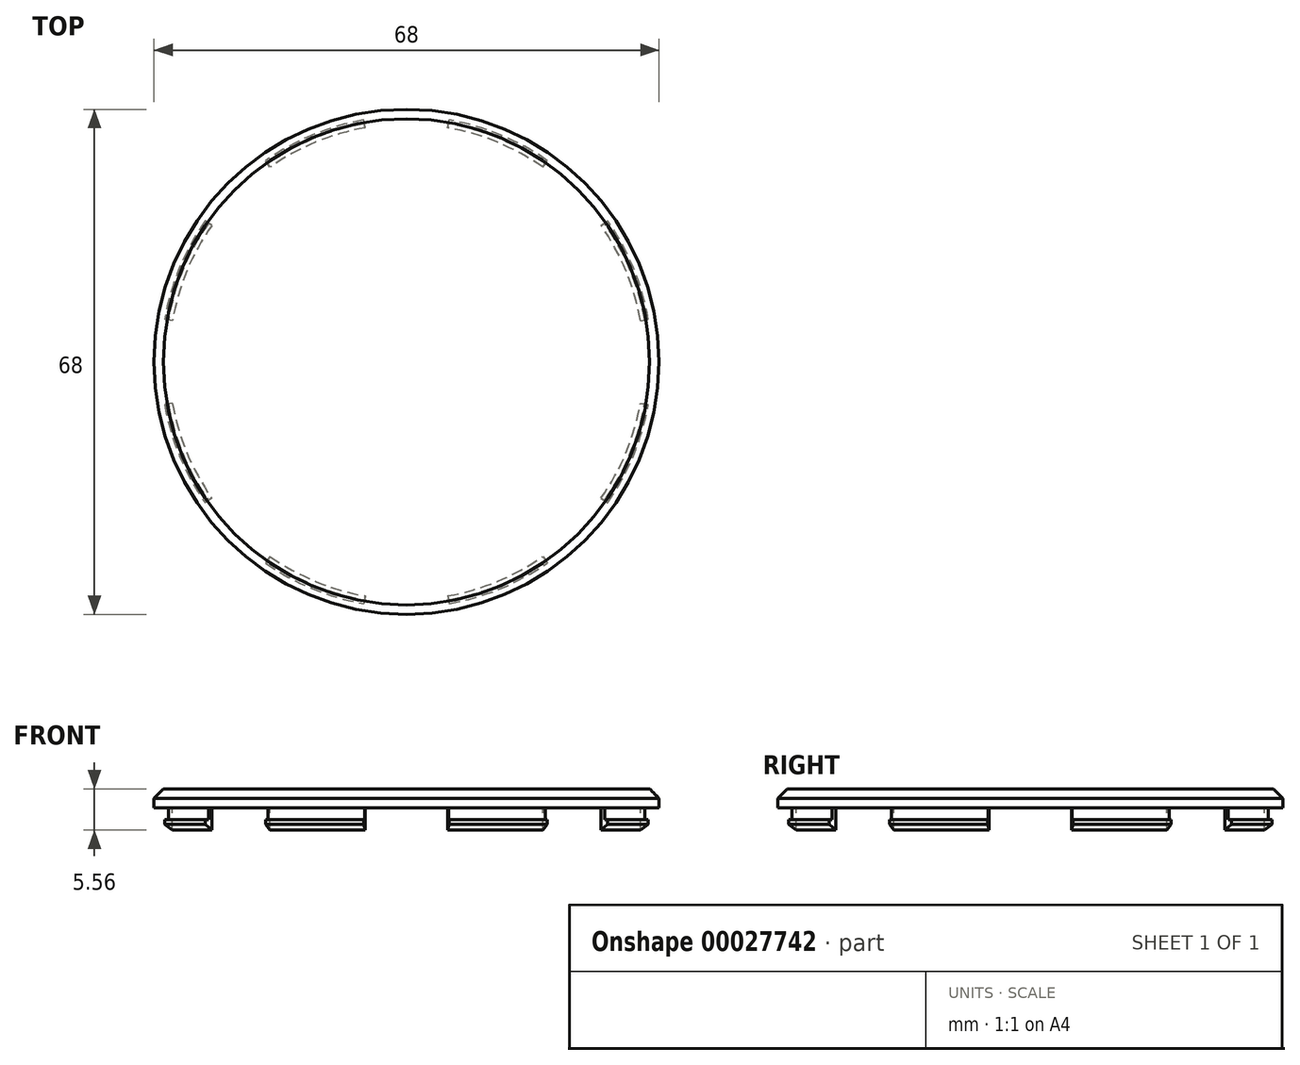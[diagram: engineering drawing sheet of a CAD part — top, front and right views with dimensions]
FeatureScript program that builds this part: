
annotation { "Feature Type Name" : "Feature", "Feature Type Description" : "" }
export const myFeature = defineFeature(function(context is Context, id is Id, definition is map)
    precondition{}
    {
        {
            var Q0;
            Q0=qCreatedBy(makeId("Top.planeOp"),FACE);
            var sketch = newSketch(context, id + "F0", { "sketchPlane" : qUnion([Q0])});
            skCircle(sketch, "E0", {"center": v(0, 0) * mm, "radius": 34 * mm});
            skSolve(sketch);
        }
        {
            var Q0;
            Q0=makeQuery(id+"F0.imprint","IMPRINT",FACE,{"disambiguationData":[TD([[makeQuery(id+"F0.imprint","IMPRINT",EDGE,{"derivedFrom":sQuery(id+"F0.wireOp",EDGE,"E0")}),1.0]])]});
            extrude(context, id + "F1", {"entities" : qUnion([Q0]), "depth" : 2.54 * mm});
        }
        {
            var Q0;
            Q0=makeQuery(id+"F1.opExtrude","CAP_EDGE",EDGE,{"disambiguationData":[OSD([sQuery(id+"F0.wireOp",EDGE,"E0")])],"isStart":false});
            chamfer(context, id + "F2", {"entities" : qUnion([Q0]), "width" : 1.27 * mm, "tangentPropagation" : true});
        }
        {
            var Q0;
            Q0=qCreatedBy(makeId("Front.planeOp"),FACE);
            var sketch = newSketch(context, id + "F3", { "sketchPlane" : qUnion([Q0])});
            skLineSegment(sketch, "E1", {"start": v(32.56, 0) * mm, "end": v(32.56, -1.61) * mm});
            skLineSegment(sketch, "E2", {"start": v(32.56, -1.61) * mm, "end": v(33.07, -1.61) * mm});
            skLineSegment(sketch, "E3", {"start": v(33.07, -1.61) * mm, "end": v(33.07, -2.24) * mm});
            skLineSegment(sketch, "E4", {"start": v(33.07, -2.24) * mm, "end": v(32, -3.02) * mm});
            skLineSegment(sketch, "E5", {"start": v(32, -3.02) * mm, "end": v(32, 0) * mm});
            skLineSegment(sketch, "E6", {"start": v(32, 0) * mm, "end": v(32.56, 0) * mm});
            skLineSegment(sketch, "E7", {"start": v(0, 0) * mm, "end": v(0, -19.48) * mm, "construction": true});
            skSolve(sketch);
        }
        {
            var Q0;
            Q0 = qSketchRegion(id + "F3", true);
            var Q1;
            Q1=sQuery(id+"F3.wireOp",EDGE,"E7");
            revolve(context, id + "F4", {"operationType" : NewBodyOperationType.ADD, "entities" : qUnion([Q0]), "axis" : qUnion([Q1]), "revolveType" : RevolveType.FULL});
        }
        {
            var Q0;
            Q0=qCreatedBy(makeId("Top.planeOp"),FACE);
            var sketch = newSketch(context, id + "F5", { "sketchPlane" : qUnion([Q0])});
            skLineSegment(sketch, "E8", {"start": v(0, 0) * mm, "end": v(6.04, 34.27) * mm, "construction": true});
            skLineSegment(sketch, "E9", {"start": v(0, 0) * mm, "end": v(-6.04, 34.27) * mm, "construction": true});
            skLineSegment(sketch, "E10", {"start": v(0, 0) * mm, "end": v(-6.04, 34.27) * mm});
            skLineSegment(sketch, "E11", {"start": v(0, 0) * mm, "end": v(6.04, 34.27) * mm});
            skArc(sketch, "E12", {"start": v(6.04, 34.27) * mm, "mid": v(0, 34.8) * mm, "end": v(-6.04, 34.27) * mm});
            skArc(sketch, "E13.1.0", {"start": v(-19.96, 28.5) * mm, "mid": v(-24.6, 24.6) * mm, "end": v(-28.5, 19.96) * mm});
            skLineSegment(sketch, "E13.1.1", {"start": v(0, 0) * mm, "end": v(-19.96, 28.5) * mm});
            skLineSegment(sketch, "E13.1.2", {"start": v(0, 0) * mm, "end": v(-28.5, 19.96) * mm});
            skLineSegment(sketch, "E13.1.3", {"start": v(0, 0) * mm, "end": v(-28.5, 19.96) * mm, "construction": true});
            skLineSegment(sketch, "E13.1.4", {"start": v(0, 0) * mm, "end": v(-19.96, 28.5) * mm, "construction": true});
            skArc(sketch, "E13.2.0", {"start": v(-34.27, 6.04) * mm, "mid": v(-34.8, 0) * mm, "end": v(-34.27, -6.04) * mm});
            skLineSegment(sketch, "E13.2.1", {"start": v(0, 0) * mm, "end": v(-34.27, 6.04) * mm});
            skLineSegment(sketch, "E13.2.2", {"start": v(0, 0) * mm, "end": v(-34.27, -6.04) * mm});
            skLineSegment(sketch, "E13.2.3", {"start": v(0, 0) * mm, "end": v(-34.27, -6.04) * mm, "construction": true});
            skLineSegment(sketch, "E13.2.4", {"start": v(0, 0) * mm, "end": v(-34.27, 6.04) * mm, "construction": true});
            skArc(sketch, "E13.3.0", {"start": v(-28.5, -19.96) * mm, "mid": v(-24.6, -24.6) * mm, "end": v(-19.96, -28.5) * mm});
            skLineSegment(sketch, "E13.3.1", {"start": v(0, 0) * mm, "end": v(-28.5, -19.96) * mm});
            skLineSegment(sketch, "E13.3.2", {"start": v(0, 0) * mm, "end": v(-19.96, -28.5) * mm});
            skLineSegment(sketch, "E13.3.3", {"start": v(0, 0) * mm, "end": v(-19.96, -28.5) * mm, "construction": true});
            skLineSegment(sketch, "E13.3.4", {"start": v(0, 0) * mm, "end": v(-28.5, -19.96) * mm, "construction": true});
            skArc(sketch, "E13.4.0", {"start": v(-6.04, -34.27) * mm, "mid": v(0, -34.8) * mm, "end": v(6.04, -34.27) * mm});
            skLineSegment(sketch, "E13.4.1", {"start": v(0, 0) * mm, "end": v(-6.04, -34.27) * mm});
            skLineSegment(sketch, "E13.4.2", {"start": v(0, 0) * mm, "end": v(6.04, -34.27) * mm});
            skLineSegment(sketch, "E13.4.3", {"start": v(0, 0) * mm, "end": v(6.04, -34.27) * mm, "construction": true});
            skLineSegment(sketch, "E13.4.4", {"start": v(0, 0) * mm, "end": v(-6.04, -34.27) * mm, "construction": true});
            skArc(sketch, "E13.5.0", {"start": v(19.96, -28.5) * mm, "mid": v(24.6, -24.6) * mm, "end": v(28.5, -19.96) * mm});
            skLineSegment(sketch, "E13.5.1", {"start": v(0, 0) * mm, "end": v(19.96, -28.5) * mm});
            skLineSegment(sketch, "E13.5.2", {"start": v(0, 0) * mm, "end": v(28.5, -19.96) * mm});
            skLineSegment(sketch, "E13.5.3", {"start": v(0, 0) * mm, "end": v(28.5, -19.96) * mm, "construction": true});
            skLineSegment(sketch, "E13.5.4", {"start": v(0, 0) * mm, "end": v(19.96, -28.5) * mm, "construction": true});
            skArc(sketch, "E13.6.0", {"start": v(34.27, -6.04) * mm, "mid": v(34.8, 0) * mm, "end": v(34.27, 6.04) * mm});
            skLineSegment(sketch, "E13.6.1", {"start": v(0, 0) * mm, "end": v(34.27, -6.04) * mm});
            skLineSegment(sketch, "E13.6.2", {"start": v(0, 0) * mm, "end": v(34.27, 6.04) * mm});
            skLineSegment(sketch, "E13.6.3", {"start": v(0, 0) * mm, "end": v(34.27, 6.04) * mm, "construction": true});
            skLineSegment(sketch, "E13.6.4", {"start": v(0, 0) * mm, "end": v(34.27, -6.04) * mm, "construction": true});
            skArc(sketch, "E13.7.0", {"start": v(28.5, 19.96) * mm, "mid": v(24.6, 24.6) * mm, "end": v(19.96, 28.5) * mm});
            skLineSegment(sketch, "E13.7.1", {"start": v(0, 0) * mm, "end": v(28.5, 19.96) * mm});
            skLineSegment(sketch, "E13.7.2", {"start": v(0, 0) * mm, "end": v(19.96, 28.5) * mm});
            skLineSegment(sketch, "E13.7.3", {"start": v(0, 0) * mm, "end": v(19.96, 28.5) * mm, "construction": true});
            skLineSegment(sketch, "E13.7.4", {"start": v(0, 0) * mm, "end": v(28.5, 19.96) * mm, "construction": true});
            skSolve(sketch);
        }
        {
            var Q0;
            Q0=makeQuery(id+"F5.imprint","IMPRINT",FACE,{"disambiguationData":[TD([[makeQuery(id+"F5.imprint","IMPRINT",EDGE,{"derivedFrom":sQuery(id+"F5.wireOp",EDGE,"E10")}),-1.0]])]});
            var Q1;
            Q1=makeQuery(id+"F5.imprint","IMPRINT",FACE,{"disambiguationData":[TD([[makeQuery(id+"F5.imprint","IMPRINT",EDGE,{"derivedFrom":sQuery(id+"F5.wireOp",EDGE,"E13.1.0")}),1.0]])]});
            var Q2;
            Q2=makeQuery(id+"F5.imprint","IMPRINT",FACE,{"disambiguationData":[TD([[makeQuery(id+"F5.imprint","IMPRINT",EDGE,{"derivedFrom":sQuery(id+"F5.wireOp",EDGE,"E13.2.0")}),1.0]])]});
            var Q3;
            Q3=makeQuery(id+"F5.imprint","IMPRINT",FACE,{"disambiguationData":[TD([[makeQuery(id+"F5.imprint","IMPRINT",EDGE,{"derivedFrom":sQuery(id+"F5.wireOp",EDGE,"E13.3.0")}),1.0]])]});
            var Q4;
            Q4=makeQuery(id+"F5.imprint","IMPRINT",FACE,{"disambiguationData":[TD([[makeQuery(id+"F5.imprint","IMPRINT",EDGE,{"derivedFrom":sQuery(id+"F5.wireOp",EDGE,"E13.4.0")}),1.0]])]});
            var Q5;
            Q5=makeQuery(id+"F5.imprint","IMPRINT",FACE,{"disambiguationData":[TD([[makeQuery(id+"F5.imprint","IMPRINT",EDGE,{"derivedFrom":sQuery(id+"F5.wireOp",EDGE,"E13.5.0")}),1.0]])]});
            var Q6;
            Q6=makeQuery(id+"F5.imprint","IMPRINT",FACE,{"disambiguationData":[TD([[makeQuery(id+"F5.imprint","IMPRINT",EDGE,{"derivedFrom":sQuery(id+"F5.wireOp",EDGE,"E13.6.0")}),1.0]])]});
            var Q7;
            Q7=makeQuery(id+"F5.imprint","IMPRINT",FACE,{"disambiguationData":[TD([[makeQuery(id+"F5.imprint","IMPRINT",EDGE,{"derivedFrom":sQuery(id+"F5.wireOp",EDGE,"E13.7.0")}),1.0]])]});
            extrude(context, id + "F6", {"entities" : qUnion([Q0, Q1, Q2, Q3, Q4, Q5, Q6, Q7]), "operationType" : NewBodyOperationType.REMOVE, "oppositeDirection" : true, "depth" : 25.4 * mm});
        }
    });
